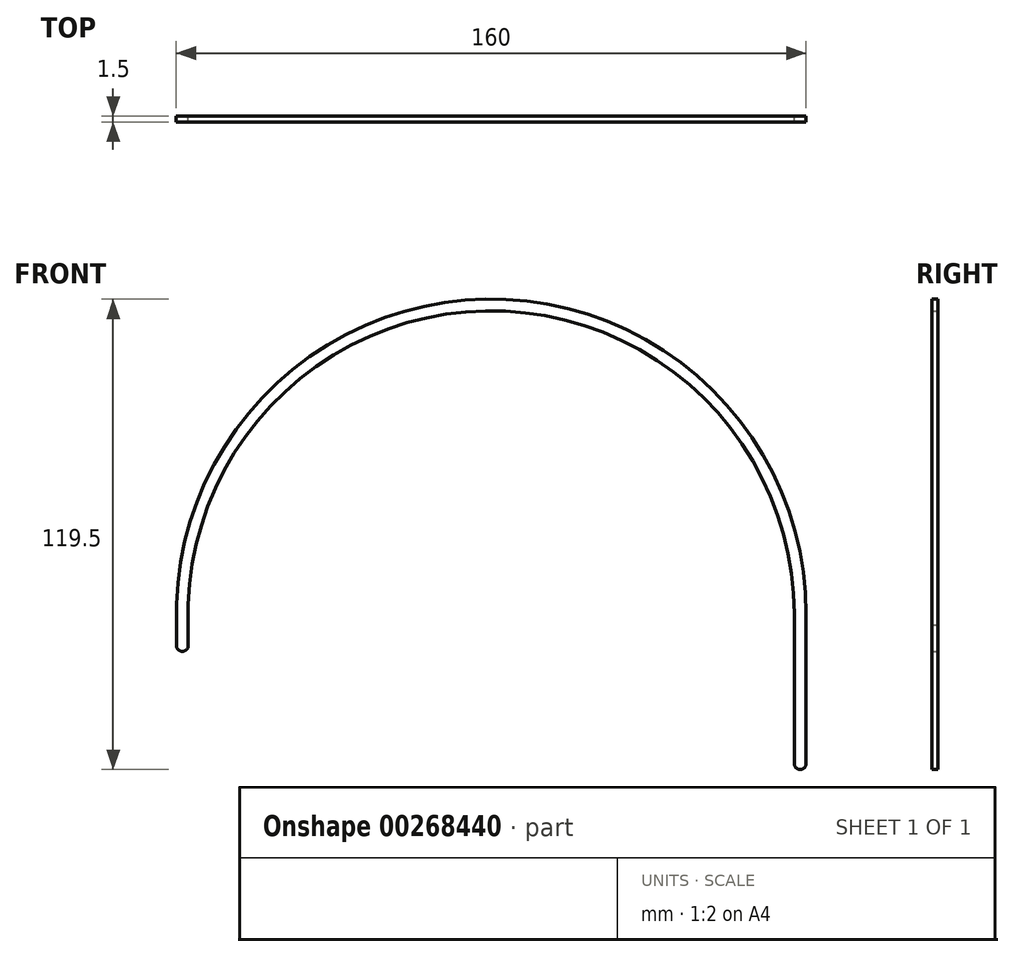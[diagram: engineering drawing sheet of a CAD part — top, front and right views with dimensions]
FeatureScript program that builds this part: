
annotation { "Feature Type Name" : "Feature", "Feature Type Description" : "" }
export const myFeature = defineFeature(function(context is Context, id is Id, definition is map)
    precondition{}
    {
        {
            var Q0;
            Q0=qCreatedBy(makeId("Front.planeOp"),FACE);
            var sketch = newSketch(context, id + "F0", { "sketchPlane" : qUnion([Q0])});
            skArc(sketch, "E0", {"start": v(80, 0) * mm, "mid": v(-1.41, 79.99) * mm, "end": v(-79.95, -2.82) * mm});
            skLineSegment(sketch, "E1", {"start": v(80, 0) * mm, "end": v(80, -38) * mm});
            skPoint(sketch, "E2.orphan", {"position": v(0, 80) * mm});
            skLineSegment(sketch, "E3", {"start": v(-79.95, -2.82) * mm, "end": v(-79.95, -8) * mm});
            skLineSegment(sketch, "E4.0", {"start": v(77, 0) * mm, "end": v(77, -38) * mm});
            skArc(sketch, "E4.1", {"start": v(77, 0) * mm, "mid": v(-1.38, 76.99) * mm, "end": v(-76.95, -2.77) * mm});
            skLineSegment(sketch, "E4.2", {"start": v(-76.95, -2.77) * mm, "end": v(-76.95, -8) * mm});
            skArc(sketch, "E5", {"start": v(77, -38) * mm, "mid": v(78.5, -39.5) * mm, "end": v(80, -38) * mm});
            skArc(sketch, "E6", {"start": v(-79.95, -8) * mm, "mid": v(-78.45, -9.5) * mm, "end": v(-76.95, -8) * mm});
            skSolve(sketch);
        }
        {
            var Q0;
            Q0=makeQuery(id+"F0.imprint","IMPRINT",FACE,{"disambiguationData":[TD([[makeQuery(id+"F0.imprint","IMPRINT",EDGE,{"derivedFrom":sQuery(id+"F0.wireOp",EDGE,"E0")}),1.0]])]});
            extrude(context, id + "F1", {"entities" : qUnion([Q0]), "depth" : 1.5 * mm});
        }
    });
